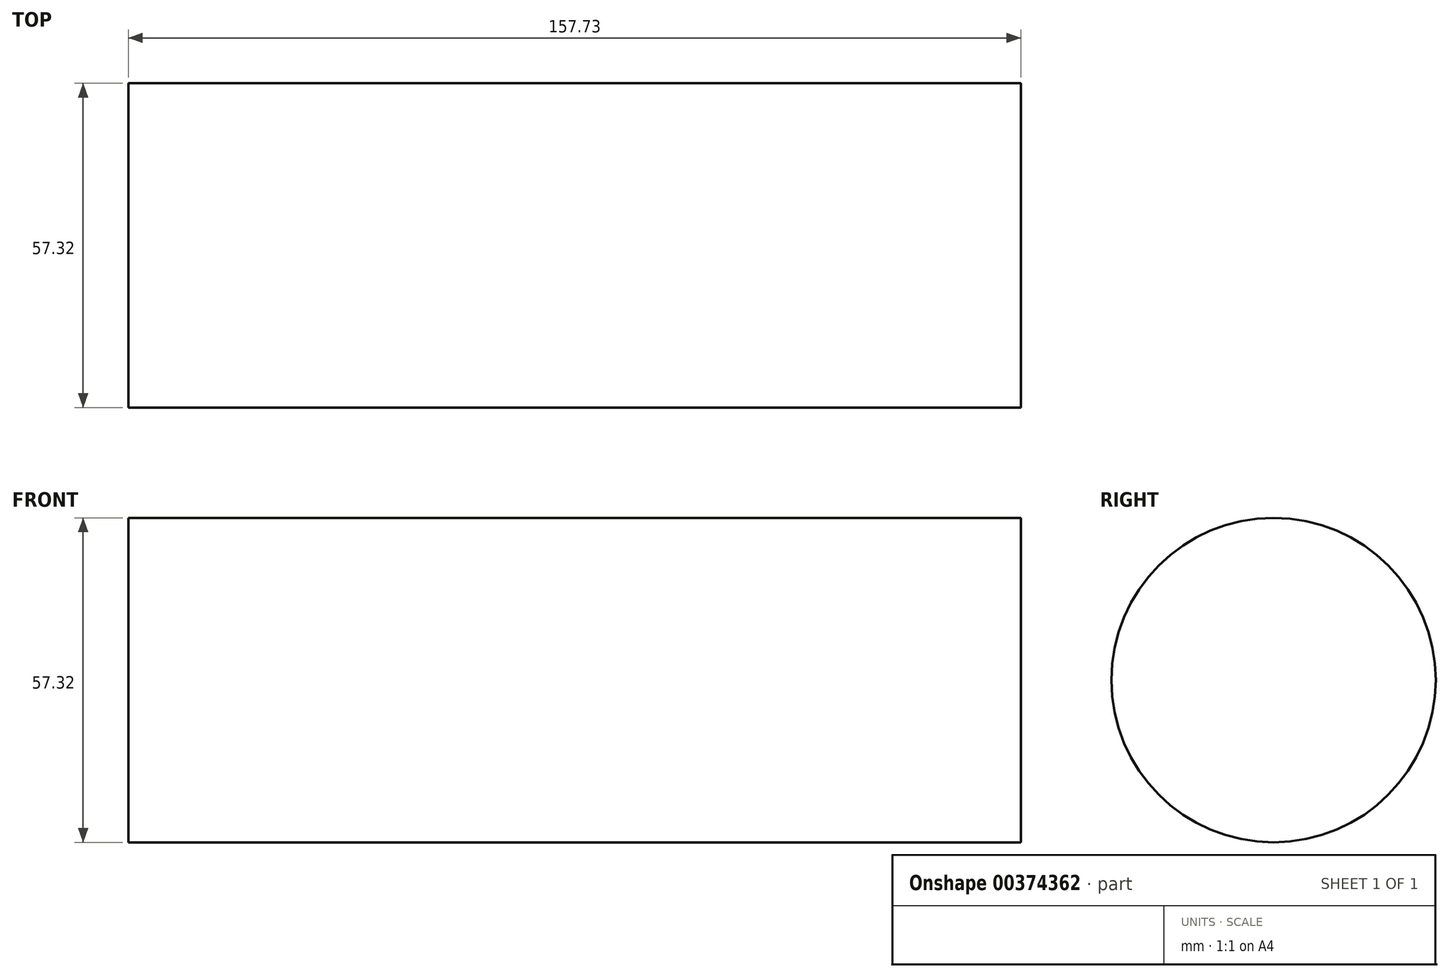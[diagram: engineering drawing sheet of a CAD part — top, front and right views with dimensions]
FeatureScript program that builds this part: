
annotation { "Feature Type Name" : "Feature", "Feature Type Description" : "" }
export const myFeature = defineFeature(function(context is Context, id is Id, definition is map)
    precondition{}
    {
        {
            var Q0;
            Q0=qCreatedBy(makeId("Top.planeOp"),FACE);
            var sketch = newSketch(context, id + "F0", { "sketchPlane" : qUnion([Q0])});
            skLineSegment(sketch, "E0", {"start": v(-97.44, 27.87) * mm, "end": v(-82.14, 27.87) * mm});
            skLineSegment(sketch, "E1", {"start": v(-82.14, 27.87) * mm, "end": v(-97.44, 27.87) * mm});
            skLineSegment(sketch, "E2", {"start": v(-97.44, 27.87) * mm, "end": v(-108.33, 21.1) * mm});
            skLineSegment(sketch, "E3", {"start": v(-108.33, 21.1) * mm, "end": v(-90.38, 4.62) * mm});
            skLineSegment(sketch, "E4", {"start": v(-90.38, 4.62) * mm, "end": v(-106.27, -5.97) * mm});
            skLineSegment(sketch, "E5", {"start": v(-106.27, -5.97) * mm, "end": v(-93.32, -15.39) * mm});
            skLineSegment(sketch, "E6", {"start": v(-93.32, -15.39) * mm, "end": v(-79.2, 4.02) * mm});
            skLineSegment(sketch, "E7", {"start": v(-79.2, 4.02) * mm, "end": v(-97.44, 19.93) * mm});
            skLineSegment(sketch, "E8", {"start": v(-97.44, 19.93) * mm, "end": v(-80.67, 22.28) * mm});
            skLineSegment(sketch, "E9", {"start": v(-80.67, 22.28) * mm, "end": v(-82.14, 27.87) * mm});
            skLineSegment(sketch, "E10", {"start": v(-63.6, -17.74) * mm, "end": v(-63.6, 27.87) * mm});
            skLineSegment(sketch, "E11", {"start": v(-63.6, 27.87) * mm, "end": v(-45.06, 14.63) * mm});
            skLineSegment(sketch, "E12", {"start": v(-45.06, 14.63) * mm, "end": v(-30.05, 31.11) * mm});
            skLineSegment(sketch, "E13", {"start": v(-30.05, 31.11) * mm, "end": v(-27.4, -16.57) * mm});
            skLineSegment(sketch, "E14", {"start": v(-27.4, -16.57) * mm, "end": v(-38.17, -17.16) * mm});
            skLineSegment(sketch, "E15", {"start": v(-38.17, -17.16) * mm, "end": v(-38.17, 14.04) * mm});
            skLineSegment(sketch, "E16", {"start": v(-38.17, 14.04) * mm, "end": v(-45.64, 0) * mm});
            skLineSegment(sketch, "E17", {"start": v(-45.64, 0) * mm, "end": v(-57.42, 11.98) * mm});
            skLineSegment(sketch, "E18", {"start": v(-57.42, 11.98) * mm, "end": v(-57.42, -18.04) * mm});
            skLineSegment(sketch, "E19", {"start": v(-57.42, -18.04) * mm, "end": v(-63.6, -17.74) * mm});
            skLineSegment(sketch, "E20", {"start": v(-12.68, 25.52) * mm, "end": v(-7.1, -14.5) * mm});
            skLineSegment(sketch, "E21", {"start": v(-7.1, -14.5) * mm, "end": v(4.1, 3.15) * mm});
            skLineSegment(sketch, "E22", {"start": v(4.1, 3.15) * mm, "end": v(12.33, -17.74) * mm});
            skLineSegment(sketch, "E23", {"start": v(12.33, -17.74) * mm, "end": v(16.75, 24.64) * mm});
            skLineSegment(sketch, "E24", {"start": v(16.75, 24.64) * mm, "end": v(7.62, 24.64) * mm});
            skLineSegment(sketch, "E25", {"start": v(7.62, 24.64) * mm, "end": v(11.74, 3.45) * mm});
            skLineSegment(sketch, "E26", {"start": v(11.74, 3.45) * mm, "end": v(3.2, 15.51) * mm});
            skLineSegment(sketch, "E27", {"start": v(3.2, 15.51) * mm, "end": v(0, 0) * mm});
            skLineSegment(sketch, "E28", {"start": v(0, 0) * mm, "end": v(-3.57, 25.52) * mm});
            skLineSegment(sketch, "E29", {"start": v(-3.57, 25.52) * mm, "end": v(-12.68, 25.52) * mm});
            skLineSegment(sketch, "E30", {"start": v(-73.6, 54.36) * mm, "end": v(-2.38, 54.36) * mm});
            skSolve(sketch);
        }
        {
            var Q0;
            Q0 = qSketchRegion(id + "F0", true);
            var Q1;
            Q1=sQuery(id+"F0.wireOp",EDGE,"E28");
            var Q2;
            Q2=sQuery(id+"F0.wireOp",EDGE,"E24");
            var Q3;
            Q3=sQuery(id+"F0.wireOp",EDGE,"E29");
            var Q4;
            Q4=sQuery(id+"F0.wireOp",EDGE,"E27");
            var Q5;
            Q5=sQuery(id+"F0.wireOp",EDGE,"E21");
            var Q6;
            Q6=sQuery(id+"F0.wireOp",EDGE,"E25");
            var Q7;
            Q7=sQuery(id+"F0.wireOp",EDGE,"E26");
            var Q8;
            Q8=sQuery(id+"F0.wireOp",EDGE,"E20");
            var Q9;
            Q9=sQuery(id+"F0.wireOp",EDGE,"E23");
            var Q10;
            Q10=sQuery(id+"F0.wireOp",EDGE,"E22");
            var Q11;
            Q11=sQuery(id+"F0.wireOp",EDGE,"E30");
            revolve(context, id + "F1", {"bodyType" : ToolBodyType.SURFACE, "entities" : qUnion([Q0]), "surfaceEntities" : qUnion([Q1, Q2, Q3, Q4, Q5, Q6, Q7, Q8, Q9, Q10]), "axis" : qUnion([Q11]), "revolveType" : RevolveType.FULL});
        }
        {
            var Q0;
            Q0=qCreatedBy(makeId("Right.planeOp"),FACE);
            var sketch = newSketch(context, id + "F2", { "sketchPlane" : qUnion([Q0])});
            skCircle(sketch, "E31", {"center": v(54, 0) * mm, "radius": 28.66 * mm});
            skSolve(sketch);
        }
        {
            var Q0;
            Q0=makeQuery(id+"F2.imprint","IMPRINT",FACE,{"disambiguationData":[TD([[makeQuery(id+"F2.imprint","IMPRINT",EDGE,{"derivedFrom":sQuery(id+"F2.wireOp",EDGE,"E31")}),1.0]])]});
            extrude(context, id + "F3", {"entities" : qUnion([Q0]), "oppositeDirection" : true, "depth" : 157.73 * mm});
        }
    });
